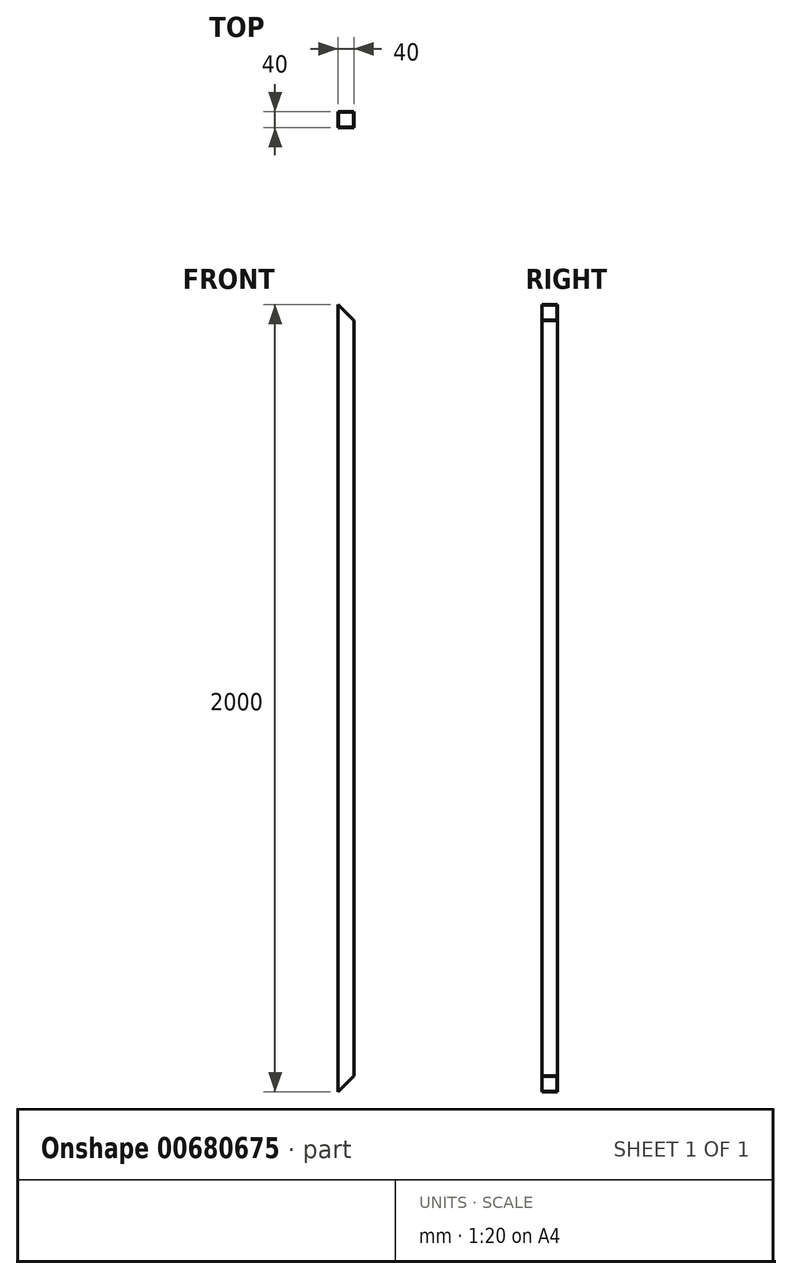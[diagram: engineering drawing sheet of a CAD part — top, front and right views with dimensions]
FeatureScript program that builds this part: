
annotation { "Feature Type Name" : "Feature", "Feature Type Description" : "" }
export const myFeature = defineFeature(function(context is Context, id is Id, definition is map)
    precondition{}
    {
        {
            var Q0;
            Q0=qCreatedBy(makeId("Top.planeOp"),FACE);
            var sketch = newSketch(context, id + "F0", { "sketchPlane" : qUnion([Q0])});
            skLineSegment(sketch, "E0.bottom", {"start": v(20, 20) * mm, "end": v(-20, 20) * mm});
            skLineSegment(sketch, "E0.top", {"start": v(20, -20) * mm, "end": v(-20, -20) * mm});
            skLineSegment(sketch, "E0.left", {"start": v(20, 20) * mm, "end": v(20, -20) * mm});
            skLineSegment(sketch, "E0.right", {"start": v(-20, 20) * mm, "end": v(-20, -20) * mm});
            skPoint(sketch, "E0.middle", {"position": v(0, 0) * mm});
            skLineSegment(sketch, "E1.bottom", {"start": v(19, 19) * mm, "end": v(-19, 19) * mm});
            skLineSegment(sketch, "E1.top", {"start": v(19, -19) * mm, "end": v(-19, -19) * mm});
            skLineSegment(sketch, "E1.left", {"start": v(19, 19) * mm, "end": v(19, -19) * mm});
            skLineSegment(sketch, "E1.right", {"start": v(-19, 19) * mm, "end": v(-19, -19) * mm});
            skSolve(sketch);
        }
        {
            var Q0;
            Q0=makeQuery(id+"F0.imprint","IMPRINT",FACE,{"disambiguationData":[TD([[makeQuery(id+"F0.imprint","IMPRINT",EDGE,{"derivedFrom":sQuery(id+"F0.wireOp",EDGE,"E0.bottom")}),1.0]])]});
            extrude(context, id + "F1", {"entities" : qUnion([Q0]), "endBound" : BoundingType.SYMMETRIC, "depth" : 2000 * mm, "offsetDistance" : 25 * mm});
        }
        {
            var Q0;
            Q0=makeQuery(id+"F1.opExtrude","SWEPT_FACE",FACE,{"disambiguationData":[OSD([sQuery(id+"F0.wireOp",EDGE,"E0.top")])]});
            var sketch = newSketch(context, id + "F2", { "sketchPlane" : qUnion([Q0])});
            skLineSegment(sketch, "E2", {"start": v(-20, 1000) * mm, "end": v(20, 960) * mm});
            skLineSegment(sketch, "E3", {"start": v(-20, -1000) * mm, "end": v(20, -960) * mm});
            skSolve(sketch);
        }
        {
            var Q0;
            {var subQ0=sQuery(id+"F2.wireOp",EDGE,"E3");Q0=makeQuery(id+"F2.imprint","IMPRINT",FACE,{"disambiguationData":[TD([[makeQuery(id+"F2.imprint","IMPRINT",EDGE,{"derivedFrom":subQ0}),-1.0]])]});}
            var Q1;
            {var subQ0=sQuery(id+"F2.wireOp",EDGE,"E2");Q1=makeQuery(id+"F2.imprint","IMPRINT",FACE,{"disambiguationData":[TD([[makeQuery(id+"F2.imprint","IMPRINT",EDGE,{"derivedFrom":subQ0}),1.0]])]});}
            extrude(context, id + "F3", {"entities" : qUnion([Q0, Q1]), "operationType" : NewBodyOperationType.REMOVE, "oppositeDirection" : true, "depth" : 100 * mm, "offsetDistance" : 25 * mm});
        }
    });
